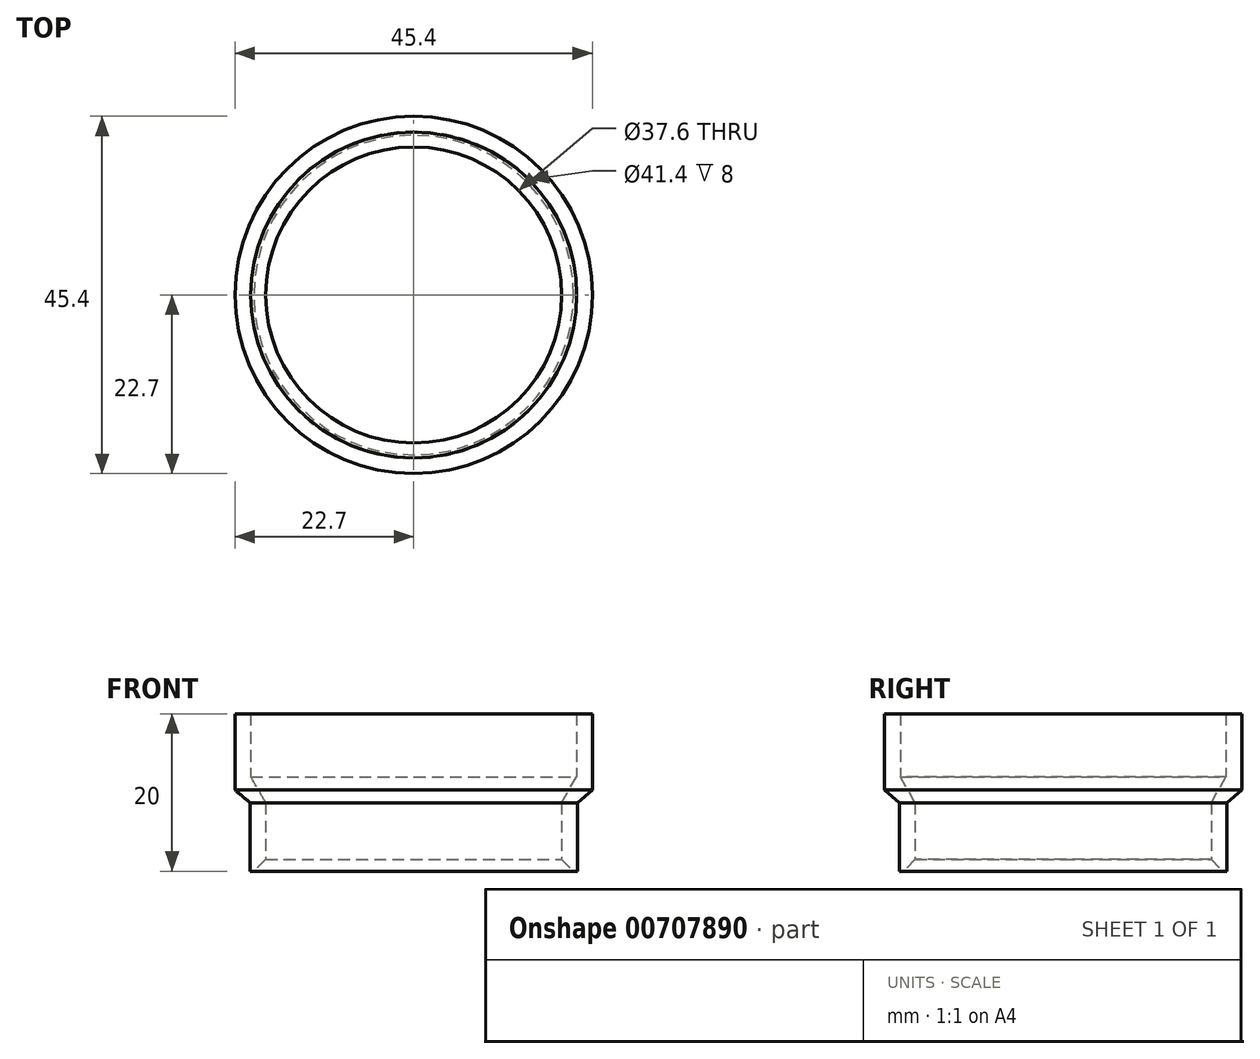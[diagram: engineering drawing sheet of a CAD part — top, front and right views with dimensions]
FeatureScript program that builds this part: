
annotation { "Feature Type Name" : "Feature", "Feature Type Description" : "" }
export const myFeature = defineFeature(function(context is Context, id is Id, definition is map)
    precondition{}
    {
        {
            var Q0;
            Q0=qCreatedBy(makeId("Front.planeOp"),FACE);
            var sketch = newSketch(context, id + "F0", { "sketchPlane" : qUnion([Q0])});
            skLineSegment(sketch, "E0", {"start": v(-22.7, 8) * mm, "end": v(-22.7, -1.7) * mm});
            skLineSegment(sketch, "E1", {"start": v(-22.7, -1.7) * mm, "end": v(-20.8, -3.3) * mm});
            skLineSegment(sketch, "E2", {"start": v(-20.8, -3.3) * mm, "end": v(-20.8, -12) * mm});
            skLineSegment(sketch, "E3", {"start": v(0, -63.3) * mm, "end": v(0, 71.6) * mm, "construction": true});
            skLineSegment(sketch, "E4", {"start": v(-22.7, 8) * mm, "end": v(-20.7, 8) * mm});
            skLineSegment(sketch, "E5", {"start": v(-20.7, 8) * mm, "end": v(-20.7, 0) * mm});
            skLineSegment(sketch, "E6", {"start": v(-20.7, 0) * mm, "end": v(-18.8, -3.3) * mm});
            skLineSegment(sketch, "E7", {"start": v(-18.8, -3.3) * mm, "end": v(-18.8, -12) * mm});
            skLineSegment(sketch, "E8", {"start": v(-18.8, -12) * mm, "end": v(-20.8, -12) * mm});
            skLineSegment(sketch, "E9", {"start": v(-18.8, -3.3) * mm, "end": v(-26.97, -3.3) * mm, "construction": true});
            skSolve(sketch);
        }
        {
            var Q0;
            Q0=makeQuery(id+"F0.imprint","IMPRINT",FACE,{"disambiguationData":[TD([[makeQuery(id+"F0.imprint","IMPRINT",EDGE,{"derivedFrom":sQuery(id+"F0.wireOp",EDGE,"E0")}),1.0]])]});
            var Q1;
            Q1=sQuery(id+"F0.wireOp",EDGE,"E3");
            revolve(context, id + "F1", {"surfaceOperationType" : NewSurfaceOperationType.NEW, "entities" : qUnion([Q0]), "axis" : qUnion([Q1]), "revolveType" : RevolveType.FULL});
        }
        {
            var Q0;
            Q0=makeQuery(id+"F1.opRevolve","SWEPT_EDGE",EDGE,{"disambiguationData":[OSD([sQuery(id+"F0.wireOp",EDGE,"E7"),sQuery(id+"F0.wireOp",EDGE,"E8")])]});
            chamfer(context, id + "F2", {"entities" : qUnion([Q0]), "width" : 1.5 * mm, "tangentPropagation" : true});
        }
    });
